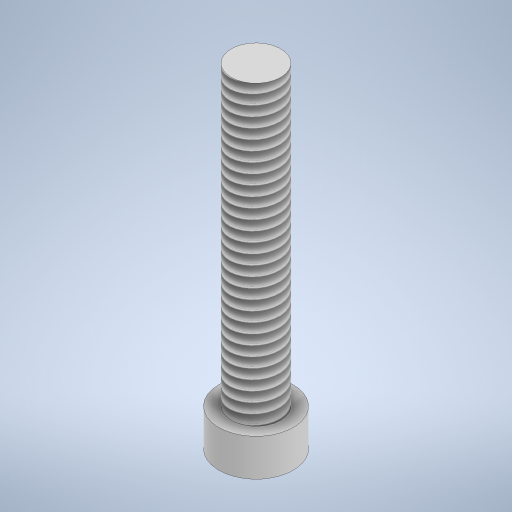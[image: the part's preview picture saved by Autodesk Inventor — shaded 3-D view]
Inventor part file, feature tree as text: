
AUTODESK INVENTOR PART (.ipt)
format: ipt  version: 2024.2 (Build 282272000, 272)  size: 282,624 bytes
history: native  units: mm
features: extrude x2, sketch x2, thread x1
ambient origin geometry x8: Origin, YZ Plane, XZ Plane, XY Plane, X Axis, Y Axis, Z Axis, Center Point
bodies: Solid1 (feature_tree)
feature tree (5):
  extrude  "Extrusion1"  Depth=1.5mm TaperAngle=0.0deg
  extrude  "Extrusion2"  Depth=12.0mm TaperAngle=0.0deg
  thread  "Thread1"  [1 undecoded]
  sketch  "Sketch1"  dims[d0=3.0mm d1=1.5mm d2=0.0mm]
  sketch  "Sketch2"  dims[d3=2.0mm d4=12.0mm d5=0.0mm d6=12.0mm d7=0.0mm]
note: 1 required parameter value undecoded (feature->parameter linkage not recoverable at this tier; creation-order binding heuristic only, values carry confidence <= 0.55)
